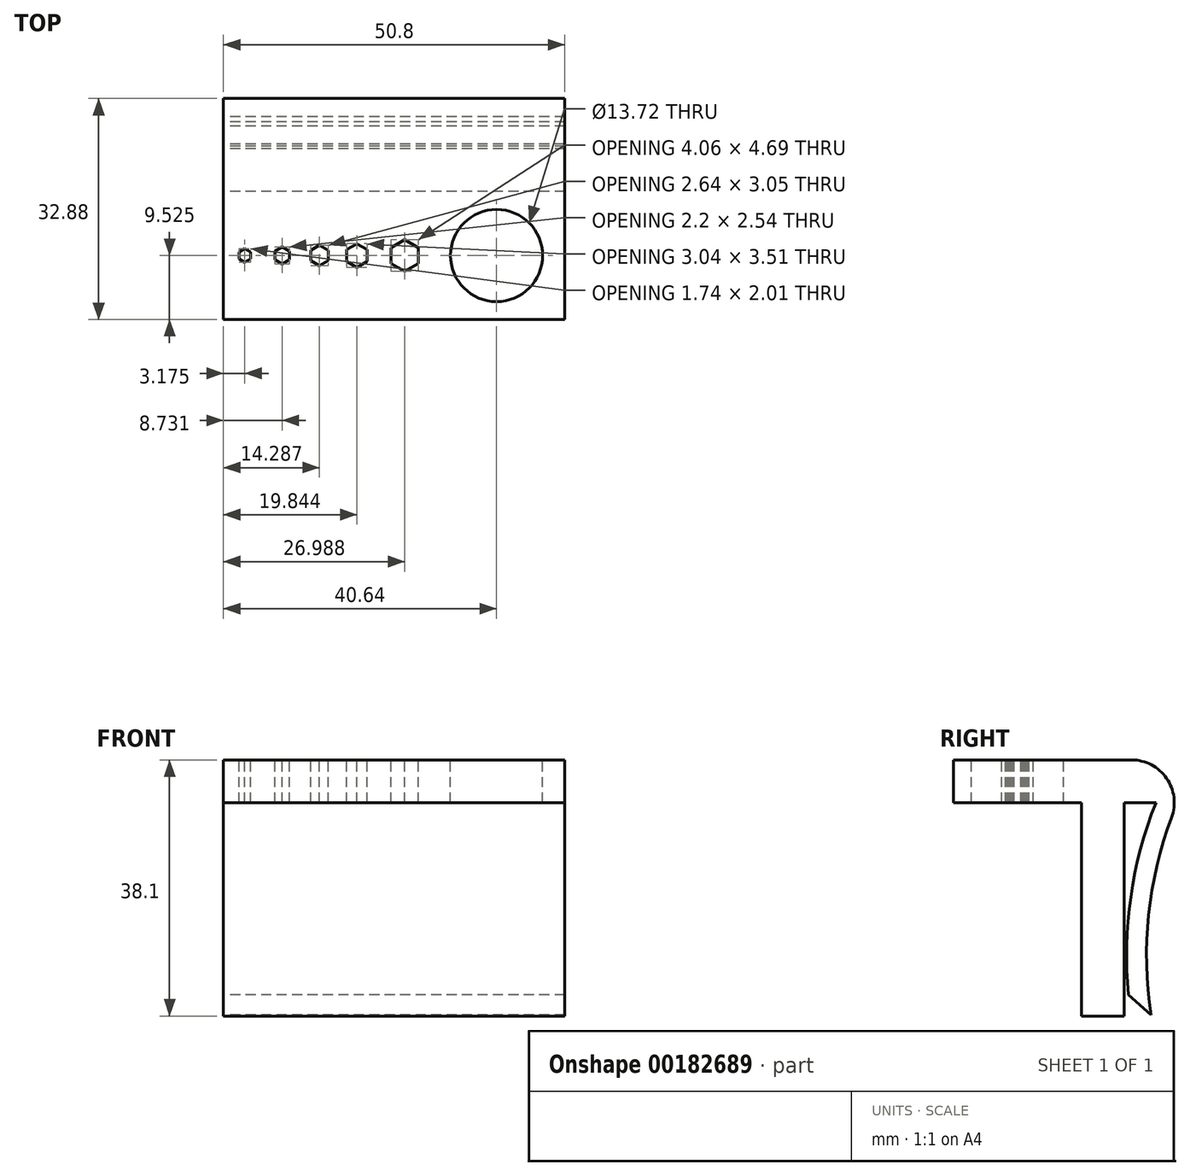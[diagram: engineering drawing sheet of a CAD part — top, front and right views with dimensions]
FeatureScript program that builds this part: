
annotation { "Feature Type Name" : "Feature", "Feature Type Description" : "" }
export const myFeature = defineFeature(function(context is Context, id is Id, definition is map)
    precondition{}
    {
        {
            var Q0;
            Q0=qCreatedBy(makeId("Right.planeOp"),FACE);
            var sketch = newSketch(context, id + "F0", { "sketchPlane" : qUnion([Q0])});
            skLineSegment(sketch, "E0", {"start": v(0, 0) * mm, "end": v(0, 50.8) * mm});
            skLineSegment(sketch, "E1", {"start": v(0, 50.8) * mm, "end": v(11.11, 50.8) * mm});
            skLineSegment(sketch, "E2", {"start": v(0, 0) * mm, "end": v(-6.35, 0) * mm});
            skLineSegment(sketch, "E3", {"start": v(-6.35, 0) * mm, "end": v(-6.35, 50.8) * mm});
            skLineSegment(sketch, "E4", {"start": v(-6.35, 50.8) * mm, "end": v(0, 50.8) * mm});
            skLineSegment(sketch, "E5", {"start": v(-6.35, 50.8) * mm, "end": v(-25.4, 50.8) * mm});
            skLineSegment(sketch, "E6", {"start": v(-25.4, 50.8) * mm, "end": v(-25.4, 44.45) * mm});
            skLineSegment(sketch, "E7", {"start": v(-25.4, 44.45) * mm, "end": v(-6.35, 44.45) * mm});
            skLineSegment(sketch, "E8", {"start": v(0, 0) * mm, "end": v(4.38, 0) * mm});
            skLineSegment(sketch, "E9", {"start": v(-6.35, 44.45) * mm, "end": v(0, 44.45) * mm});
            skLineSegment(sketch, "E10", {"start": v(0, 44.45) * mm, "end": v(4.76, 44.45) * mm});
            skArc(sketch, "E11", {"start": v(4.76, 44.45) * mm, "mid": v(0.4, 22.26) * mm, "end": v(4.38, 0) * mm});
            skLineSegment(sketch, "E12", {"start": v(4.38, 0) * mm, "end": v(7.55, 0) * mm});
            skArc(sketch, "E13", {"start": v(11.11, 50.8) * mm, "mid": v(3.5, 25.8) * mm, "end": v(7.55, 0) * mm});
            skLineSegment(sketch, "E14", {"start": v(-6.35, 12.7) * mm, "end": v(0, 12.7) * mm});
            skLineSegment(sketch, "E15", {"start": v(0, 12.7) * mm, "end": v(1.07, 12.7) * mm, "construction": true});
            skLineSegment(sketch, "E16", {"start": v(1.07, 12.7) * mm, "end": v(4.06, 12.7) * mm});
            skSolve(sketch);
        }
        {
            var Q0;
            {var subQ0=sQuery(id+"F0.wireOp",EDGE,"E5");Q0=makeQuery(id+"F0.imprint","IMPRINT",FACE,{"disambiguationData":[TD([[makeQuery(id+"F0.imprint","IMPRINT",EDGE,{"derivedFrom":subQ0}),1.0]])]});}
            var Q1;
            {var subQ0=sQuery(id+"F0.wireOp",EDGE,"E4");Q1=makeQuery(id+"F0.imprint","IMPRINT",FACE,{"disambiguationData":[TD([[makeQuery(id+"F0.imprint","IMPRINT",EDGE,{"derivedFrom":subQ0}),-1.0]])]});}
            var Q2;
            {var subQ0=sQuery(id+"F0.wireOp",EDGE,"E9");Q2=makeQuery(id+"F0.imprint","IMPRINT",FACE,{"disambiguationData":[TD([[makeQuery(id+"F0.imprint","IMPRINT",EDGE,{"derivedFrom":subQ0}),-1.0]])]});}
            var Q3;
            {var subQ4=sQuery(id+"F0.wireOp",EDGE,"E1");Q3=makeQuery(id+"F0.imprint","IMPRINT",FACE,{"disambiguationData":[TD([[makeQuery(id+"F0.imprint","IMPRINT",EDGE,{"derivedFrom":subQ4}),-1.0]])]});}
            extrude(context, id + "F1", {"entities" : qUnion([Q0, Q1, Q2, Q3]), "depth" : 50.8 * mm});
        }
        {
            var Q0;
            Q0=makeQuery(id+"F1.opExtrude","SWEPT_FACE",FACE,{"disambiguationData":[OSD([sQuery(id+"F0.wireOp",EDGE,"E1"),sQuery(id+"F0.wireOp",EDGE,"E4"),sQuery(id+"F0.wireOp",EDGE,"E5")])]});
            var sketch = newSketch(context, id + "F2", { "sketchPlane" : qUnion([Q0])});
            skLineSegment(sketch, "E17", {"start": v(3.17, -15.88) * mm, "end": v(8.73, -15.88) * mm});
            skLineSegment(sketch, "E18", {"start": v(8.73, -15.88) * mm, "end": v(14.29, -15.88) * mm});
            skLineSegment(sketch, "E19", {"start": v(14.29, -15.88) * mm, "end": v(19.84, -15.88) * mm});
            skLineSegment(sketch, "E20", {"start": v(40.64, -15.88) * mm, "end": v(50.8, -15.88) * mm});
            skCircle(sketch, "E21.cCircle", {"center": v(3.17, -15.88) * mm, "radius": 1 * mm, "construction": true});
            skLineSegment(sketch, "E21.0", {"start": v(3.18, -14.87) * mm, "end": v(4.04, -15.37) * mm});
            skLineSegment(sketch, "E21.1", {"start": v(4.04, -15.37) * mm, "end": v(4.04, -16.38) * mm});
            skLineSegment(sketch, "E21.2", {"start": v(4.04, -16.38) * mm, "end": v(3.18, -16.88) * mm});
            skLineSegment(sketch, "E21.3", {"start": v(3.17, -16.88) * mm, "end": v(2.3, -16.38) * mm});
            skLineSegment(sketch, "E21.4", {"start": v(2.3, -16.38) * mm, "end": v(2.3, -15.37) * mm});
            skLineSegment(sketch, "E21.5", {"start": v(2.3, -15.37) * mm, "end": v(3.17, -14.87) * mm});
            skCircle(sketch, "E22.cCircle", {"center": v(14.29, -15.88) * mm, "radius": 1.52 * mm, "construction": true});
            skLineSegment(sketch, "E22.0", {"start": v(14.29, -14.35) * mm, "end": v(15.6, -15.11) * mm});
            skLineSegment(sketch, "E22.1", {"start": v(15.6, -15.11) * mm, "end": v(15.6, -16.64) * mm});
            skLineSegment(sketch, "E22.2", {"start": v(15.6, -16.64) * mm, "end": v(14.29, -17.4) * mm});
            skLineSegment(sketch, "E22.3", {"start": v(14.29, -17.4) * mm, "end": v(12.97, -16.64) * mm});
            skLineSegment(sketch, "E22.4", {"start": v(12.97, -16.64) * mm, "end": v(12.97, -15.11) * mm});
            skLineSegment(sketch, "E22.5", {"start": v(12.97, -15.11) * mm, "end": v(14.29, -14.35) * mm});
            skCircle(sketch, "E23.cCircle", {"center": v(19.84, -15.88) * mm, "radius": 1.75 * mm, "construction": true});
            skLineSegment(sketch, "E23.0", {"start": v(19.84, -14.12) * mm, "end": v(21.36, -15) * mm});
            skLineSegment(sketch, "E23.1", {"start": v(21.36, -15) * mm, "end": v(21.36, -16.75) * mm});
            skLineSegment(sketch, "E23.2", {"start": v(21.36, -16.75) * mm, "end": v(19.84, -17.63) * mm});
            skLineSegment(sketch, "E23.3", {"start": v(19.84, -17.63) * mm, "end": v(18.33, -16.75) * mm});
            skLineSegment(sketch, "E23.4", {"start": v(18.33, -16.75) * mm, "end": v(18.33, -15) * mm});
            skLineSegment(sketch, "E23.5", {"start": v(18.33, -15) * mm, "end": v(19.84, -14.12) * mm});
            skCircle(sketch, "E24.cCircle", {"center": v(8.73, -15.88) * mm, "radius": 1.27 * mm, "construction": true});
            skLineSegment(sketch, "E24.0", {"start": v(8.73, -14.6) * mm, "end": v(9.83, -15.24) * mm});
            skLineSegment(sketch, "E24.1", {"start": v(9.83, -15.24) * mm, "end": v(9.83, -16.5) * mm});
            skLineSegment(sketch, "E24.2", {"start": v(9.83, -16.51) * mm, "end": v(8.73, -17.15) * mm});
            skLineSegment(sketch, "E24.3", {"start": v(8.73, -17.14) * mm, "end": v(7.63, -16.5) * mm});
            skLineSegment(sketch, "E24.4", {"start": v(7.63, -16.51) * mm, "end": v(7.63, -15.24) * mm});
            skLineSegment(sketch, "E24.5", {"start": v(7.63, -15.24) * mm, "end": v(8.73, -14.6) * mm});
            skCircle(sketch, "E25", {"center": v(40.64, -15.88) * mm, "radius": 6.86 * mm});
            skLineSegment(sketch, "E26", {"start": v(3.17, -15.88) * mm, "end": v(0, -15.88) * mm});
            skLineSegment(sketch, "E27", {"start": v(40.64, -15.88) * mm, "end": v(19.84, -15.88) * mm});
            skLineSegment(sketch, "E28", {"start": v(19.84, -15.88) * mm, "end": v(26.99, -15.88) * mm});
            skCircle(sketch, "E29.cCircle", {"center": v(26.99, -15.88) * mm, "radius": 2.03 * mm, "construction": true});
            skLineSegment(sketch, "E29.0", {"start": v(24.96, -14.7) * mm, "end": v(26.99, -13.53) * mm});
            skLineSegment(sketch, "E29.1", {"start": v(26.99, -13.53) * mm, "end": v(29.02, -14.7) * mm});
            skLineSegment(sketch, "E29.2", {"start": v(29.02, -14.7) * mm, "end": v(29.02, -17.05) * mm});
            skLineSegment(sketch, "E29.3", {"start": v(29.02, -17.05) * mm, "end": v(26.99, -18.22) * mm});
            skLineSegment(sketch, "E29.4", {"start": v(26.99, -18.22) * mm, "end": v(24.96, -17.05) * mm});
            skLineSegment(sketch, "E29.5", {"start": v(24.96, -17.05) * mm, "end": v(24.96, -14.7) * mm});
            skPoint(sketch, "E29.0.midPoint", {"position": v(25.97, -14.12) * mm});
            skSolve(sketch);
        }
        {
            var Q0;
            Q0 = qSketchRegion(id + "F2", true);
            extrude(context, id + "F3", {"entities" : qUnion([Q0]), "operationType" : NewBodyOperationType.REMOVE, "endBound" : BoundingType.THROUGH_ALL, "oppositeDirection" : true, "depth" : 25.4 * mm});
        }
        {
            var Q0;
            Q0=makeQuery(id+"F1.opExtrude","SWEPT_EDGE",EDGE,{"disambiguationData":[OSD([sQuery(id+"F0.wireOp",EDGE,"E1"),sQuery(id+"F0.wireOp",EDGE,"E13")])]});
            fillet(context, id + "F4", {"entities" : qUnion([Q0]), "radius" : 6.35 * mm, "tangentPropagation" : true, "allowEdgeOverflow" : false});
        }
        {
            var Q0;
            Q0=makeQuery(id+"F1.opExtrude","SWEPT_EDGE",EDGE,{"disambiguationData":[OSD([sQuery(id+"F0.wireOp",EDGE,"E11"),sQuery(id+"F0.wireOp",EDGE,"E16")])]});
            chamfer(context, id + "F5", {"entities" : qUnion([Q0]), "width" : 3.17 * mm, "tangentPropagation" : true});
        }
    });
